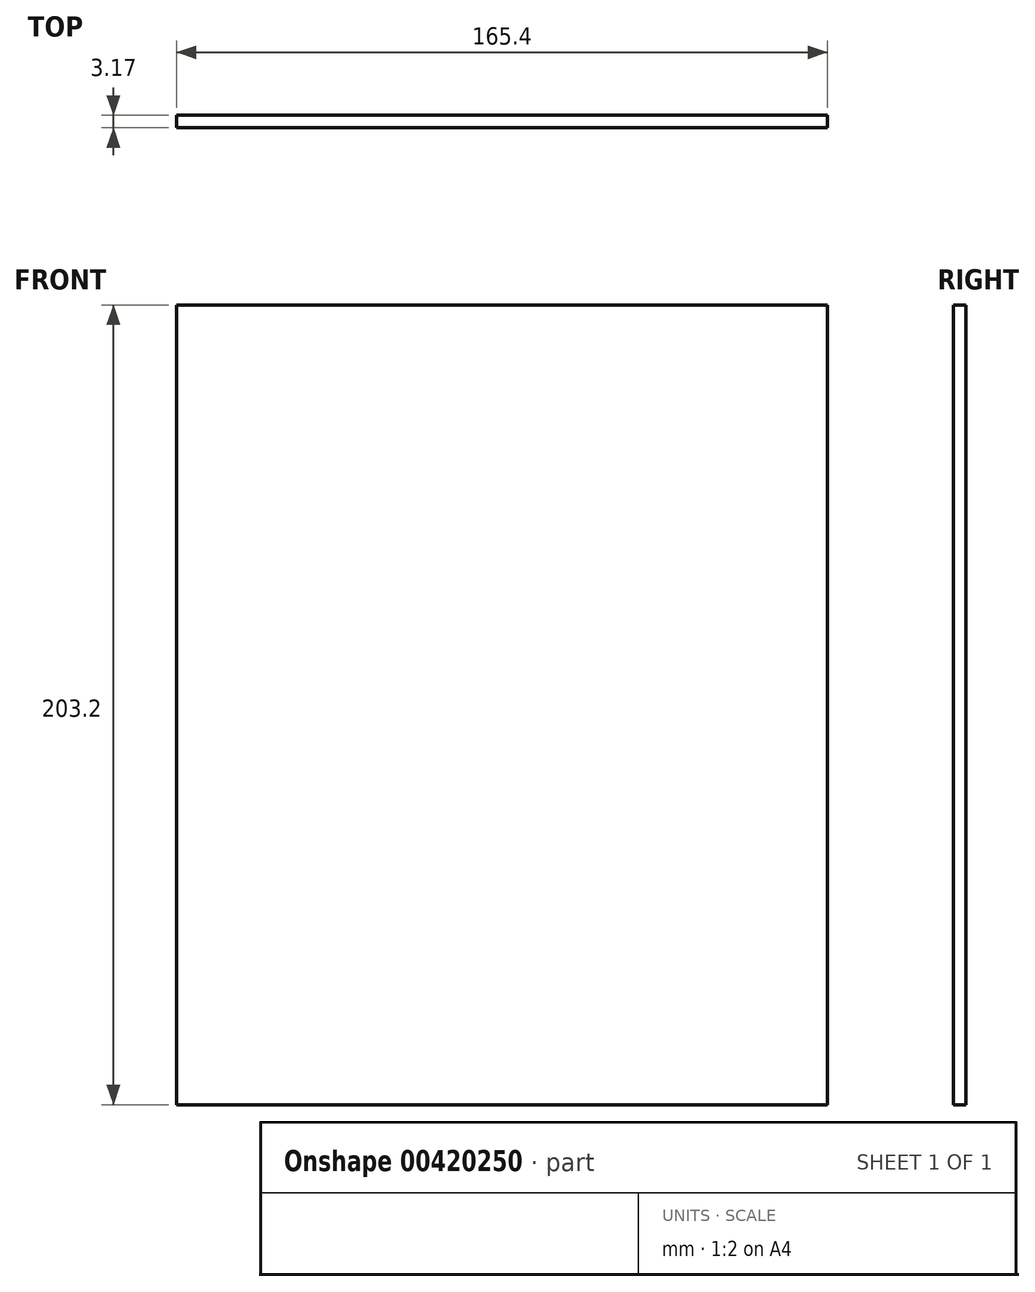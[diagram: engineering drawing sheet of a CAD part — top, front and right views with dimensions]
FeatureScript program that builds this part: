
annotation { "Feature Type Name" : "Feature", "Feature Type Description" : "" }
export const myFeature = defineFeature(function(context is Context, id is Id, definition is map)
    precondition{}
    {
        {
            var Q0;
            Q0=qCreatedBy(makeId("Front.planeOp"),FACE);
            var sketch = newSketch(context, id + "F0", { "sketchPlane" : qUnion([Q0])});
            skLineSegment(sketch, "E0.bottom", {"start": v(-82.7, -101.6) * mm, "end": v(82.7, -101.6) * mm});
            skLineSegment(sketch, "E0.top", {"start": v(-82.7, 101.6) * mm, "end": v(82.7, 101.6) * mm});
            skLineSegment(sketch, "E0.left", {"start": v(-82.7, -101.6) * mm, "end": v(-82.7, 101.6) * mm});
            skLineSegment(sketch, "E0.right", {"start": v(82.7, -101.6) * mm, "end": v(82.7, 101.6) * mm});
            skLineSegment(sketch, "E1", {"start": v(0, 219.74) * mm, "end": v(0, -172.48) * mm, "construction": true});
            skPoint(sketch, "E2", {"position": v(0, 101.6) * mm});
            skLineSegment(sketch, "E3", {"start": v(-229.2, 0) * mm, "end": v(267, 0) * mm, "construction": true});
            skPoint(sketch, "E4", {"position": v(82.7, 0) * mm});
            skSolve(sketch);
        }
        {
            var Q0;
            Q0 = qSketchRegion(id + "F0", true);
            extrude(context, id + "F1", {"entities" : qUnion([Q0]), "depth" : 3.17 * mm});
        }
    });
